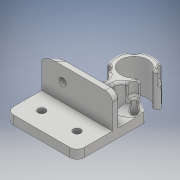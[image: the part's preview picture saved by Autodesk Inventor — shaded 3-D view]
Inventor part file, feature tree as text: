
AUTODESK INVENTOR PART (.ipt)
format: ipt  version: 2018 (Build 220112000, 112)  size: 657,408 bytes
history: native  units: mm
features: extrude x10, sketch x10, fillet x5, projected_geometry x3, chamfer x2
ambient origin geometry x8: Origin, YZ Plane, XZ Plane, XY Plane, X Axis, Y Axis, Z Axis, Center Point
bodies: Solid1 (feature_tree)
feature tree (30):
  extrude  "Extrusion1"  Depth=7.0mm
  extrude  "Extrusion2"  Depth=40.0mm
  extrude  "Extrusion3"  Depth=5.0mm TaperAngle=0.0deg
  extrude  "Extrusion4"  Depth=14.0mm TaperAngle=0.0deg
  extrude  "Extrusion5"  Depth=10.0mm
  chamfer  "Chamfer1"  Distance=15.0mm
  extrude  "Extrusion6"  Depth=5.0mm
  fillet  "Fillet1"  Radius=14.0mm
  fillet  "Fillet2"  Radius=20.0mm
  chamfer  "Chamfer2"  Distance=4.0mm
  fillet  "Fillet3"  Radius=2.0mm
  extrude  "Extrusion7"  Depth=10.0mm TaperAngle=45.0deg
  extrude  "Extrusion8"  Depth=10.0mm
  fillet  "Fillet4"  Radius=1.4mm
  fillet  "Fillet5"  Radius=3.3mm
  extrude  "Extrusion9"  TaperAngle=45.0deg  [1 undecoded]
  extrude  "Extrusion10"  Depth=10.0mm
  sketch  "Sketch1"  dims[d0=8.2mm d1=7.0mm]
  sketch  "Sketch2"  dims[d2=20.0mm d4=40.0mm]
  sketch  "Sketch3"  dims[d5=35.0mm d6=5.0mm d7=0.0mm]
  sketch  "Sketch4"  dims[d8=15.2mm d9=14.0mm d10=0.0mm]
  sketch  "Sketch5"  dims[d11=4.2mm d12=10.0mm]
  projected_geometry  "Projected Loop1"
  sketch  "Sketch6"  dims[d13=10.0mm]
  sketch  "Sketch7"  dims[d14=20.0mm d15=15.0mm d16=0.0mm]
  sketch  "Sketch8"  dims[d17=18.0mm d18=0.0mm d19=5.0mm d20=14.0mm d21=0.0mm]
  sketch  "Sketch9"  dims[d22=1.0mm d23=2.0mm d24=45.0deg d25=20.0mm d26=0.0mm]
  projected_geometry  "Projected Loop2"
  sketch  "Sketch10"  dims[d27=4.0mm d31=4.0mm d32=2.0mm d33=1.0mm d34=2.0mm d35=45.0deg d39=23.5mm d40=1.4mm d41=3.3mm d42=45.0deg d43=12.0mm d44=40.0mm d46=360.0deg d48=10.0mm d49=0.0mm d50=5.8mm d51=40.0mm d53=360.0deg d55=8.0mm d56=0.0mm d57=2.0mm d58=0.5mm d59=10.0mm d60=4.2mm d61=5.0mm d62=8.0mm d63=0.0mm d64=10.0mm d65=0.0mm]
  projected_geometry  "Projected Loop3"
note: 1 required parameter value undecoded (feature->parameter linkage not recoverable at this tier; creation-order binding heuristic only, values carry confidence <= 0.55)
